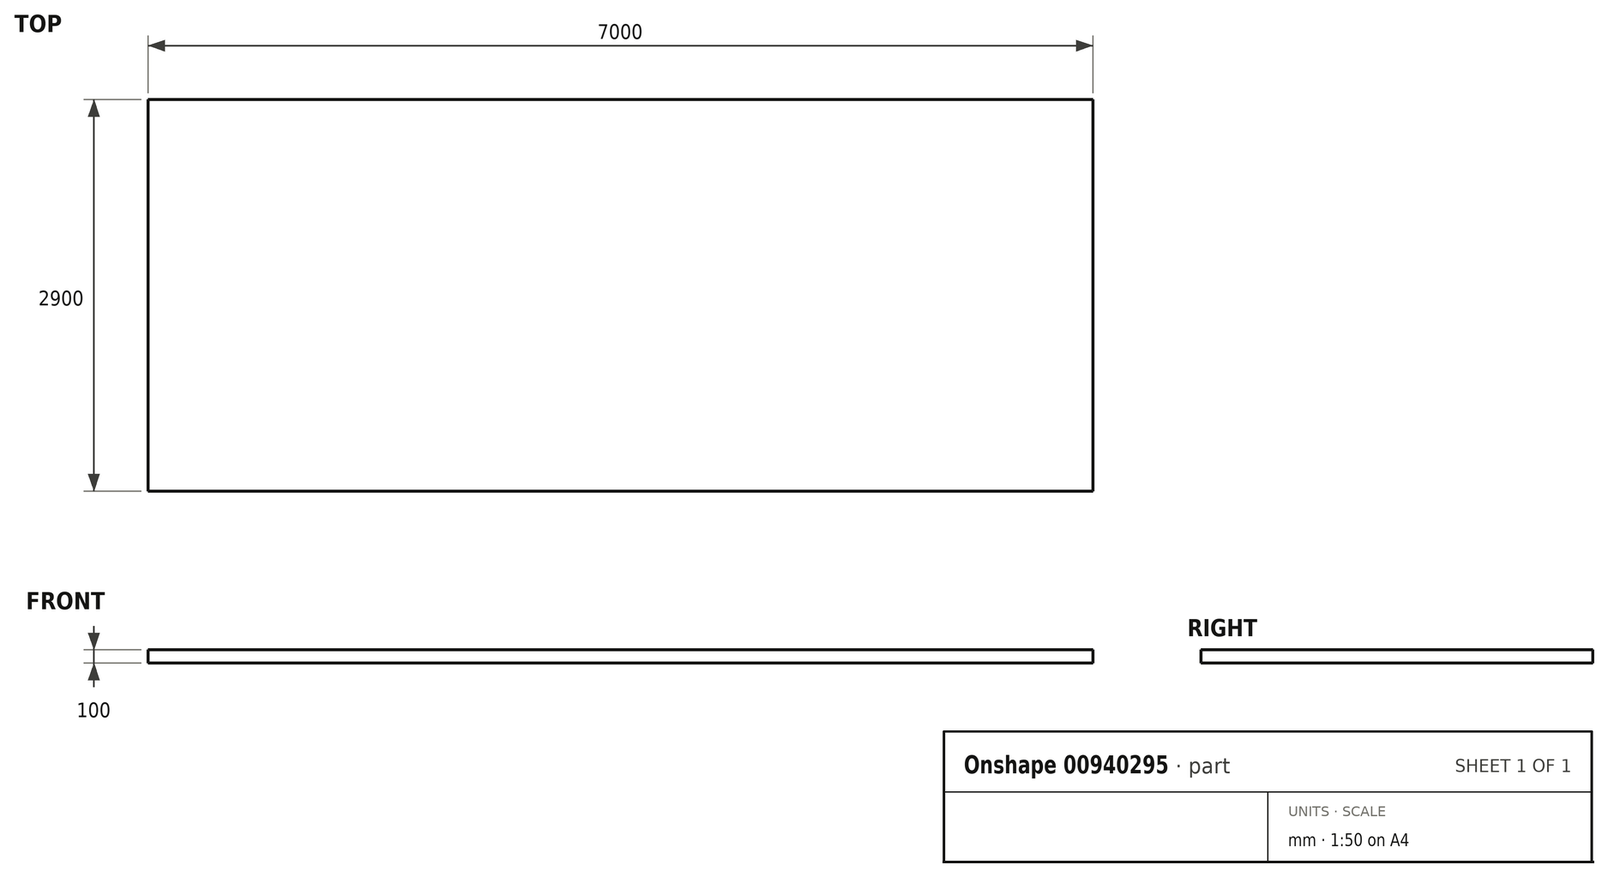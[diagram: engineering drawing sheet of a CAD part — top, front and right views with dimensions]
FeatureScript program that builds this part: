
annotation { "Feature Type Name" : "Feature", "Feature Type Description" : "" }
export const myFeature = defineFeature(function(context is Context, id is Id, definition is map)
    precondition{}
    {
        {
            var Q0;
            Q0=qCreatedBy(makeId("Top.planeOp"),FACE);
            var sketch = newSketch(context, id + "F0", { "sketchPlane" : qUnion([Q0])});
            skLineSegment(sketch, "E0.bottom", {"start": v(-3500, 1450) * mm, "end": v(3500, 1450) * mm});
            skLineSegment(sketch, "E0.top", {"start": v(-3500, -1450) * mm, "end": v(3500, -1450) * mm});
            skLineSegment(sketch, "E0.left", {"start": v(-3500, 1450) * mm, "end": v(-3500, -1450) * mm});
            skLineSegment(sketch, "E0.right", {"start": v(3500, 1450) * mm, "end": v(3500, -1450) * mm});
            skSolve(sketch);
        }
        {
            var Q0;
            Q0 = qSketchRegion(id + "F0", true);
            extrude(context, id + "F1", {"entities" : qUnion([Q0]), "depth" : 100 * mm, "offsetDistance" : 25 * mm});
        }
    });
